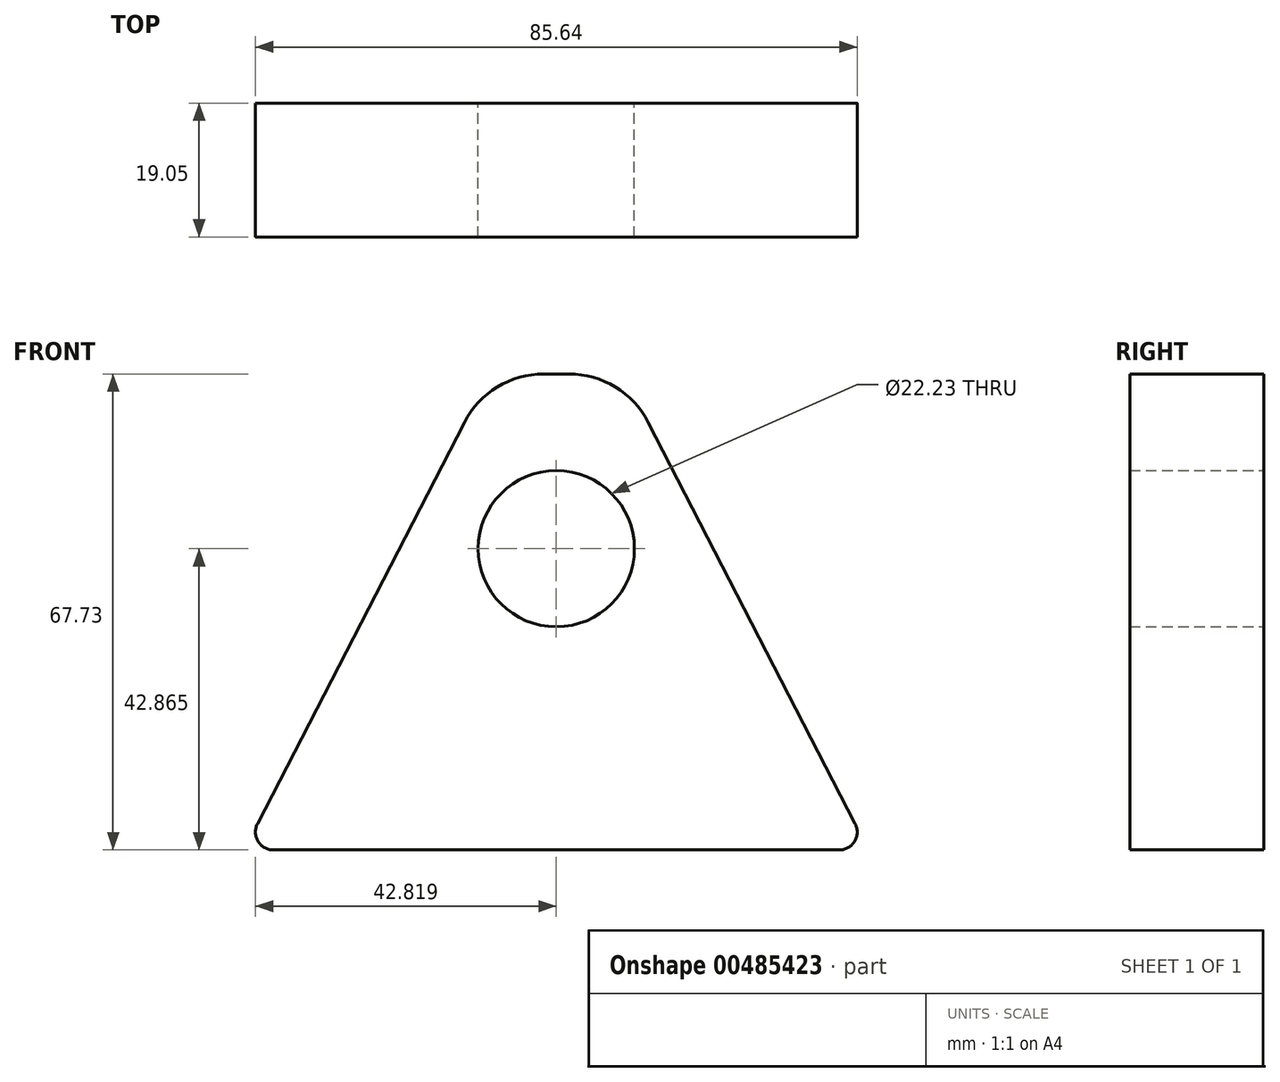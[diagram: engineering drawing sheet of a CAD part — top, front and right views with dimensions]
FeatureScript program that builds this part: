
annotation { "Feature Type Name" : "Feature", "Feature Type Description" : "" }
export const myFeature = defineFeature(function(context is Context, id is Id, definition is map)
    precondition{}
    {
        {
            var Q0;
            Q0=qCreatedBy(makeId("Front.planeOp"),FACE);
            var sketch = newSketch(context, id + "F0", { "sketchPlane" : qUnion([Q0])});
            skLineSegment(sketch, "E0", {"start": v(-50.51, 12.45) * mm, "end": v(38.39, 12.45) * mm});
            skLineSegment(sketch, "E1", {"start": v(38.39, 12.45) * mm, "end": v(3.46, 80.18) * mm});
            skLineSegment(sketch, "E2", {"start": v(3.46, 80.18) * mm, "end": v(-15.59, 80.18) * mm});
            skLineSegment(sketch, "E3", {"start": v(-15.59, 80.18) * mm, "end": v(-50.51, 12.45) * mm});
            skCircle(sketch, "E4", {"center": v(-6.06, 55.32) * mm, "radius": 11.11 * mm});
            skPoint(sketch, "E4.centerSnap0", {"position": v(-6.06, 12.45) * mm});
            skSolve(sketch);
        }
        {
            var Q0;
            Q0=makeQuery(id+"F0.imprint","IMPRINT",FACE,{"disambiguationData":[TD([[makeQuery(id+"F0.imprint","IMPRINT",EDGE,{"derivedFrom":sQuery(id+"F0.wireOp",EDGE,"E0")}),1.0]])]});
            extrude(context, id + "F1", {"entities" : qUnion([Q0]), "depth" : 19.05 * mm});
        }
        {
            var Q0;
            Q0=makeQuery(id+"F1.opExtrude","SWEPT_EDGE",EDGE,{"disambiguationData":[OSD([sQuery(id+"F0.wireOp",EDGE,"E2"),sQuery(id+"F0.wireOp",EDGE,"E3")])]});
            var Q1;
            Q1=makeQuery(id+"F1.opExtrude","SWEPT_EDGE",EDGE,{"disambiguationData":[OSD([sQuery(id+"F0.wireOp",EDGE,"E1"),sQuery(id+"F0.wireOp",EDGE,"E2")])]});
            fillet(context, id + "F2", {"entities" : qUnion([Q0, Q1]), "radius" : 12.7 * mm, "tangentPropagation" : true, "allowEdgeOverflow" : false});
        }
        {
            var Q0;
            Q0=makeQuery(id+"F1.opExtrude","SWEPT_EDGE",EDGE,{"disambiguationData":[OSD([sQuery(id+"F0.wireOp",EDGE,"E0"),sQuery(id+"F0.wireOp",EDGE,"E3")])]});
            var Q1;
            Q1=makeQuery(id+"F1.opExtrude","SWEPT_EDGE",EDGE,{"disambiguationData":[OSD([sQuery(id+"F0.wireOp",EDGE,"E0"),sQuery(id+"F0.wireOp",EDGE,"E1")])]});
            fillet(context, id + "F3", {"entities" : qUnion([Q0, Q1]), "radius" : 2.54 * mm, "tangentPropagation" : true, "allowEdgeOverflow" : false});
        }
    });
